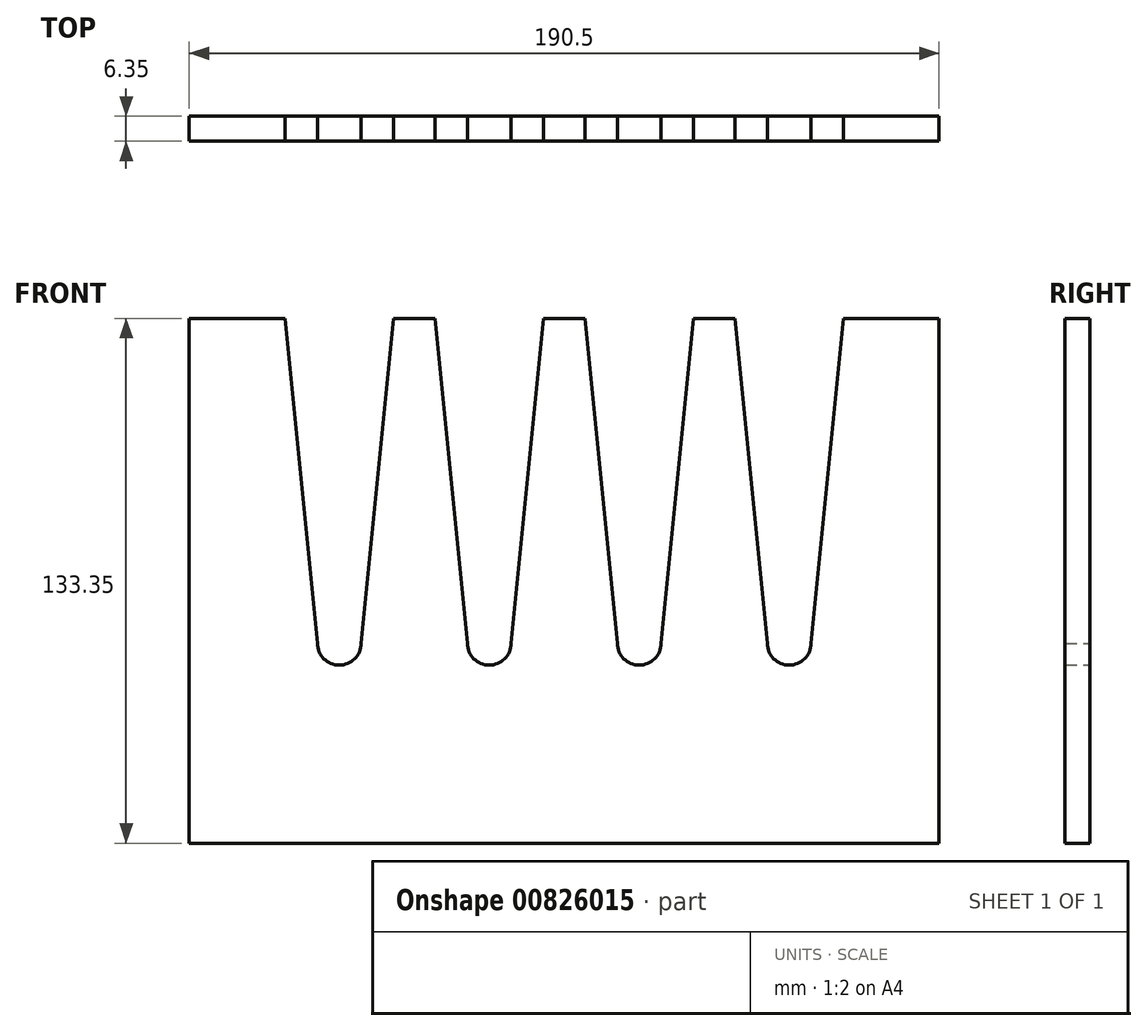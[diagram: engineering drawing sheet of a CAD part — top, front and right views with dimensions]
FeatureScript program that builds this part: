
annotation { "Feature Type Name" : "Feature", "Feature Type Description" : "" }
export const myFeature = defineFeature(function(context is Context, id is Id, definition is map)
    precondition{}
    {
        {
            var Q0;
            Q0=qCreatedBy(makeId("Front.planeOp"),FACE);
            var sketch = newSketch(context, id + "F0", { "sketchPlane" : qUnion([Q0])});
            skLineSegment(sketch, "E0.top", {"start": v(-70.64, -23.4) * mm, "end": v(119.86, -23.4) * mm});
            skLineSegment(sketch, "E0.left", {"start": v(-70.64, 21.04) * mm, "end": v(-70.64, -23.4) * mm});
            skLineSegment(sketch, "E0.right", {"start": v(119.86, 21.04) * mm, "end": v(119.86, -23.4) * mm, "construction": true});
            skLineSegment(sketch, "E1", {"start": v(-32.54, -23.4) * mm, "end": v(-32.54, 21.04) * mm, "construction": true});
            skLineSegment(sketch, "E2", {"start": v(5.56, -23.4) * mm, "end": v(5.56, 21.04) * mm, "construction": true});
            skLineSegment(sketch, "E3", {"start": v(43.66, 21.04) * mm, "end": v(43.66, -23.4) * mm, "construction": true});
            skLineSegment(sketch, "E4", {"start": v(81.76, 21.04) * mm, "end": v(81.76, -23.4) * mm, "construction": true});
            skPoint(sketch, "E5", {"position": v(-32.54, -10.7) * mm});
            skPoint(sketch, "E6", {"position": v(5.56, -10.7) * mm});
            skPoint(sketch, "E7", {"position": v(43.66, -10.7) * mm});
            skPoint(sketch, "E8", {"position": v(81.76, -10.7) * mm});
            skPoint(sketch, "E9", {"position": v(-38.1, -10.7) * mm});
            skPoint(sketch, "E10", {"position": v(-26.99, -10.7) * mm});
            skPoint(sketch, "E11", {"position": v(-41.27, 21.04) * mm});
            skPoint(sketch, "E12", {"position": v(-23.81, 21.04) * mm});
            skLineSegment(sketch, "E13", {"start": v(-38.1, -10.7) * mm, "end": v(-41.27, 21.04) * mm});
            skLineSegment(sketch, "E14", {"start": v(-26.99, -10.7) * mm, "end": v(-23.81, 21.04) * mm});
            skArc(sketch, "E15", {"start": v(-38.1, -10.7) * mm, "mid": v(-32.54, -16.27) * mm, "end": v(-26.99, -10.7) * mm});
            skPoint(sketch, "E16", {"position": v(5.56, 21.04) * mm});
            skPoint(sketch, "E17", {"position": v(14.29, 21.04) * mm});
            skPoint(sketch, "E18", {"position": v(-3.18, 21.04) * mm});
            skPoint(sketch, "E19", {"position": v(0, -10.7) * mm});
            skPoint(sketch, "E20", {"position": v(11.11, -10.7) * mm});
            skLineSegment(sketch, "E21", {"start": v(0, -10.7) * mm, "end": v(-3.18, 21.04) * mm});
            skLineSegment(sketch, "E22", {"start": v(14.29, 21.04) * mm, "end": v(11.11, -10.7) * mm});
            skArc(sketch, "E23", {"start": v(0, -10.7) * mm, "mid": v(5.56, -16.27) * mm, "end": v(11.11, -10.7) * mm});
            skArc(sketch, "E24.MirrorCS", {"start": v(87.31, -10.7) * mm, "mid": v(81.76, -16.27) * mm, "end": v(76.2, -10.7) * mm});
            skPoint(sketch, "E25.MirrorP", {"position": v(90.49, 21.04) * mm});
            skPoint(sketch, "E26.MirrorP", {"position": v(38.1, -10.7) * mm});
            skLineSegment(sketch, "E27.MirrorCS", {"start": v(49.21, -10.7) * mm, "end": v(52.39, 21.04) * mm});
            skArc(sketch, "E28.MirrorCS", {"start": v(49.21, -10.7) * mm, "mid": v(43.66, -16.27) * mm, "end": v(38.1, -10.7) * mm});
            skPoint(sketch, "E29.MirrorP", {"position": v(52.39, 21.04) * mm});
            skPoint(sketch, "E30.MirrorP", {"position": v(43.66, 21.04) * mm});
            skPoint(sketch, "E31.MirrorP", {"position": v(73.03, 21.04) * mm});
            skPoint(sketch, "E32.MirrorP", {"position": v(87.31, -10.7) * mm});
            skPoint(sketch, "E33.MirrorP", {"position": v(49.21, -10.7) * mm});
            skPoint(sketch, "E34.MirrorP", {"position": v(76.2, -10.7) * mm});
            skLineSegment(sketch, "E35.MirrorCS", {"start": v(76.2, -10.7) * mm, "end": v(73.03, 21.04) * mm});
            skLineSegment(sketch, "E36.MirrorCS", {"start": v(119.86, 21.04) * mm, "end": v(119.86, -23.4) * mm});
            skLineSegment(sketch, "E37.MirrorCS", {"start": v(81.76, -23.4) * mm, "end": v(81.76, 21.04) * mm, "construction": true});
            skPoint(sketch, "E38.MirrorP", {"position": v(34.93, 21.04) * mm});
            skLineSegment(sketch, "E39.MirrorCS", {"start": v(43.66, -23.4) * mm, "end": v(43.66, 21.04) * mm, "construction": true});
            skLineSegment(sketch, "E40.MirrorCS", {"start": v(34.93, 21.04) * mm, "end": v(38.1, -10.7) * mm});
            skLineSegment(sketch, "E41.MirrorCS", {"start": v(87.31, -10.7) * mm, "end": v(90.49, 21.04) * mm});
            skLineSegment(sketch, "E42.left", {"start": v(-70.64, 21.04) * mm, "end": v(-70.64, 21.04) * mm});
            skLineSegment(sketch, "E42.right", {"start": v(119.86, 21.04) * mm, "end": v(119.86, 21.04) * mm});
            skLineSegment(sketch, "E43.bottom", {"start": v(119.86, 71.84) * mm, "end": v(-70.64, 71.84) * mm});
            skLineSegment(sketch, "E43.left", {"start": v(119.86, 71.84) * mm, "end": v(119.86, 21.04) * mm});
            skLineSegment(sketch, "E43.right", {"start": v(-70.64, 71.84) * mm, "end": v(-70.64, 21.04) * mm});
            skLineSegment(sketch, "E44", {"start": v(-41.27, 21.04) * mm, "end": v(-46.36, 71.84) * mm});
            skLineSegment(sketch, "E45", {"start": v(-23.81, 21.04) * mm, "end": v(-18.73, 71.84) * mm});
            skLineSegment(sketch, "E46", {"start": v(-3.18, 21.04) * mm, "end": v(-8.26, 71.84) * mm});
            skLineSegment(sketch, "E47", {"start": v(14.29, 21.04) * mm, "end": v(19.37, 71.84) * mm});
            skLineSegment(sketch, "E48", {"start": v(34.93, 21.04) * mm, "end": v(29.85, 71.84) * mm});
            skLineSegment(sketch, "E49", {"start": v(52.39, 21.04) * mm, "end": v(57.47, 71.84) * mm});
            skLineSegment(sketch, "E50", {"start": v(73.03, 21.04) * mm, "end": v(67.95, 71.84) * mm});
            skLineSegment(sketch, "E51", {"start": v(90.49, 21.04) * mm, "end": v(95.57, 71.84) * mm});
            skLineSegment(sketch, "E52.bottom", {"start": v(-70.64, -23.4) * mm, "end": v(119.86, -23.4) * mm, "construction": true});
            skLineSegment(sketch, "E52.top", {"start": v(-70.64, -61.5) * mm, "end": v(119.86, -61.5) * mm});
            skLineSegment(sketch, "E52.left", {"start": v(-70.64, -23.4) * mm, "end": v(-70.64, -61.5) * mm});
            skLineSegment(sketch, "E52.right", {"start": v(119.86, -23.4) * mm, "end": v(119.86, -61.5) * mm});
            skSolve(sketch);
        }
        {
            var Q0;
            Q0=makeQuery(id+"F0.imprint","IMPRINT",FACE,{"disambiguationData":[TD([[makeQuery(id+"F0.imprint","IMPRINT",EDGE,{"derivedFrom":sQuery(id+"F0.wireOp",EDGE,"E0.top")}),1.0]])]});
            var Q1;
            Q1=makeQuery(id+"F0.imprint","IMPRINT",FACE,{"disambiguationData":[TD([[makeQuery(id+"F0.imprint","IMPRINT",EDGE,{"derivedFrom":sQuery(id+"F0.wireOp",EDGE,"E0.top")}),-1.0]])]});
            extrude(context, id + "F1", {"entities" : qUnion([Q0, Q1]), "depth" : 6.35 * mm, "offsetDistance" : 25.4 * mm});
        }
    });
